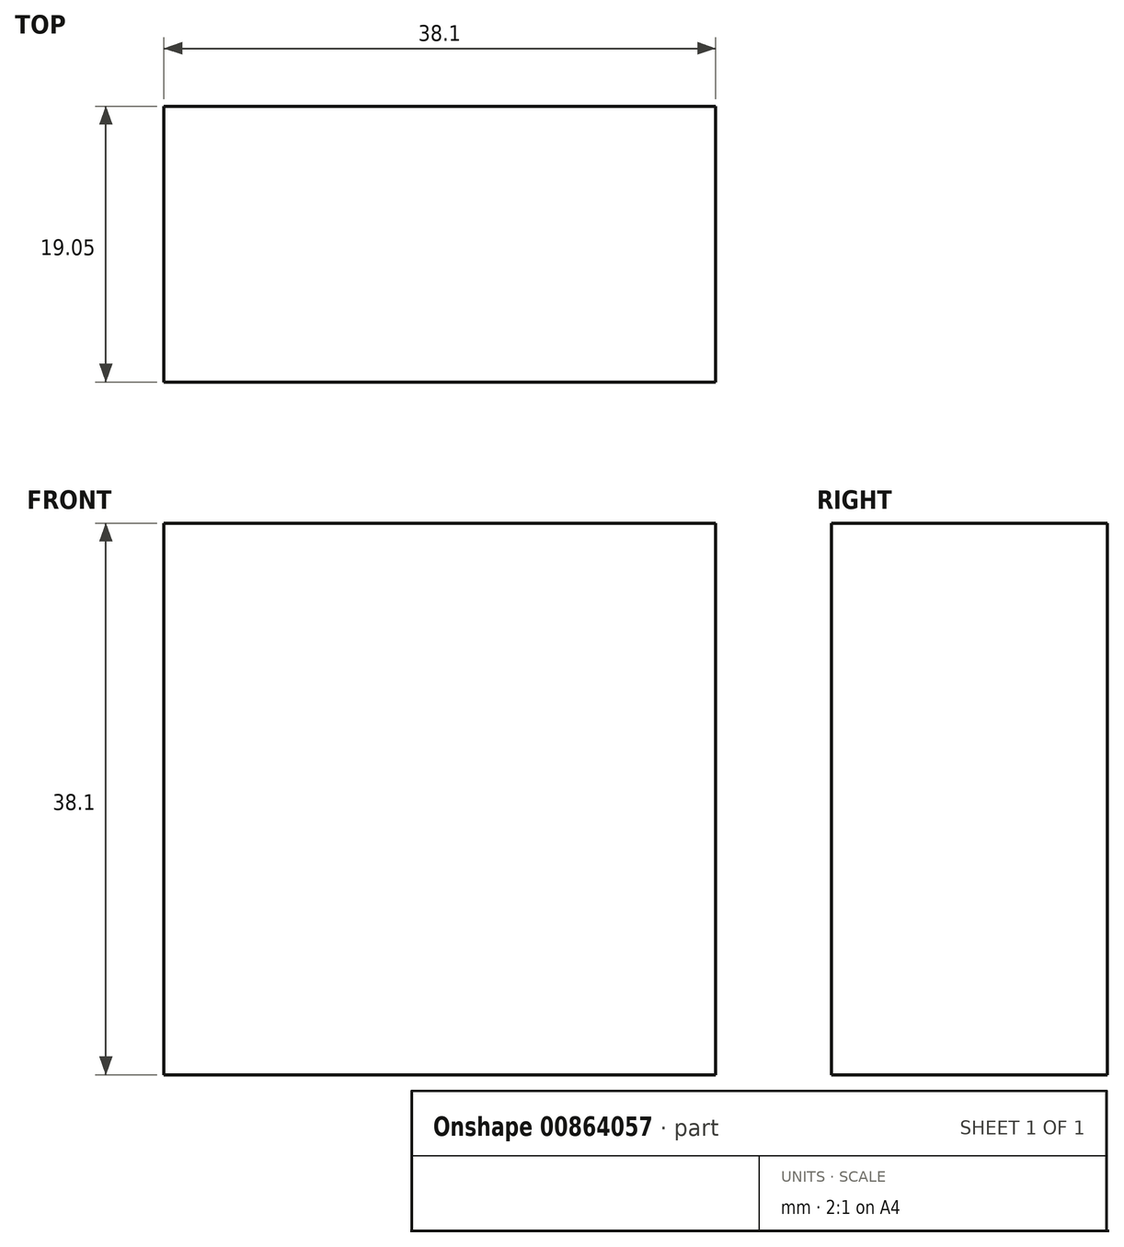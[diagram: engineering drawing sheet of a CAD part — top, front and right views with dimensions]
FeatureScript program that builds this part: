
annotation { "Feature Type Name" : "Feature", "Feature Type Description" : "" }
export const myFeature = defineFeature(function(context is Context, id is Id, definition is map)
    precondition{}
    {
        {
            var Q0;
            Q0=qCreatedBy(makeId("Front.planeOp"),FACE);
            var sketch = newSketch(context, id + "F0", { "sketchPlane" : qUnion([Q0])});
            skLineSegment(sketch, "E0", {"start": v(0, 0) * mm, "end": v(0, 38.1) * mm});
            skLineSegment(sketch, "E1", {"start": v(0, 38.1) * mm, "end": v(38.1, 38.1) * mm});
            skLineSegment(sketch, "E2", {"start": v(38.1, 38.1) * mm, "end": v(38.1, 0) * mm});
            skLineSegment(sketch, "E3", {"start": v(0, 0) * mm, "end": v(38.1, 0) * mm});
            skSolve(sketch);
        }
        {
            var Q0;
            Q0 = qSketchRegion(id + "F0", true);
            extrude(context, id + "F1", {"entities" : qUnion([Q0]), "depth" : 19.05 * mm, "offsetDistance" : 25.4 * mm});
        }
    });
